# Revit family: 0047690 Lighting Fixture_Sylvania_Sylproof Superia LED_Surface Mounted
name_source: partatom
category: Lighting Fixtures
revit_build: Autodesk Revit 2015 (Build: 20140606_1530(x64)
units: mm (PartAtom-declared; Revit-internal decimal feet)

## types (1)
- Sylproof Superia LED 1265mm TWIN NW
    Apparent Load = 46 VA
    Assembly Code = D5020200
    Body Material = Polycarbonate_Body_Sylvania_Brite White
    Bracket-Diffuser Material = Stainless Steel_Bracket_Sylvania_Grey
    Bracket-Mounting Material = Stainless Steel_Bracket_Sylvania_Grey
    Catalog Number = 0047690 Sylproof Superia LED 1265mm TWIN NW
    Color Filter = 16777215
    Default Elevation = 0 mm  [stored 0 ft]
    Description = Weather and Vandal resistant LED luminaire with heat resistant robust polycarbonate body (IK08). UV stabilised polycarbonate diffuser with linear prisms designed to optimise light output and to reduce glare. Stainless steel diffuser clips and fixing brackets for surface mounting. Retained diffuser for easy maintenance. As Sylvania Sylproof Superia LED
    Diffuser Brackets Length = 1105 mm
    Diffuser Material = Polycarbonate_Diffuser_Sylvania_Clear
    Dimming Lamp Color Temperature Shift = <None>
    Electrical Protection = CLASS I
    Emit Shape Visible in Rendering = No
    Emit from Rectangle Length = 1245 mm  [stored 4.08465 ft]
    Emit from Rectangle Width = 110 mm  [stored 0.360892 ft]
    Height = 97 mm  [stored 0.318241 ft]
    IK Rating = IK08
    IP Rating = IP65
    Lamp = 46W LED
    Lamp - Single = No
    Lamp - Twin = Yes
    Lamp Comments = Integrated LED
    Lamp Material = Acrylic High Luminance Glass_Lamp_Sylvania_White
    Length = 1265 mm  [stored 4.15026 ft]
    Length Help = 1205 mm
    Life = 50 000h
    Manufacturer = Feilo-Sylvania Group
    Model = Sylproof Superia LED 1265mm TWIN NW
    Mounting Brackets Length = 800 mm  [stored 2.62467 ft]
    Mounting Brackets Width = 54 mm  [stored 0.177165 ft]
    Number of Diffuser Brackets = 5
    Photometric Web File = 0047689_SYLPROOFSUPERIALED24W4KNW-163364.ies
    Product Family = SYLPROOF SUPERIA LED
    Side Void Width = 70 mm  [stored 0.229659 ft]
    Tilt Angle = -90.00°
    Voltage = 240 V
    Voltage Comments = UNV (Universal Voltage; 220-240 Volt)
    Weight = 2.50 kg
    Width = 138 mm  [stored 0.452756 ft]
    Width Help = 70 mm  [stored 0.229659 ft]

note: [stored X ft] marks values corroborated as IEEE doubles in the binary element streams (Revit-internal decimal feet)

## geometry (parser evidence)
native form markers: Blend x5, Sweep x13
no freeform markers — native parametric forms only
